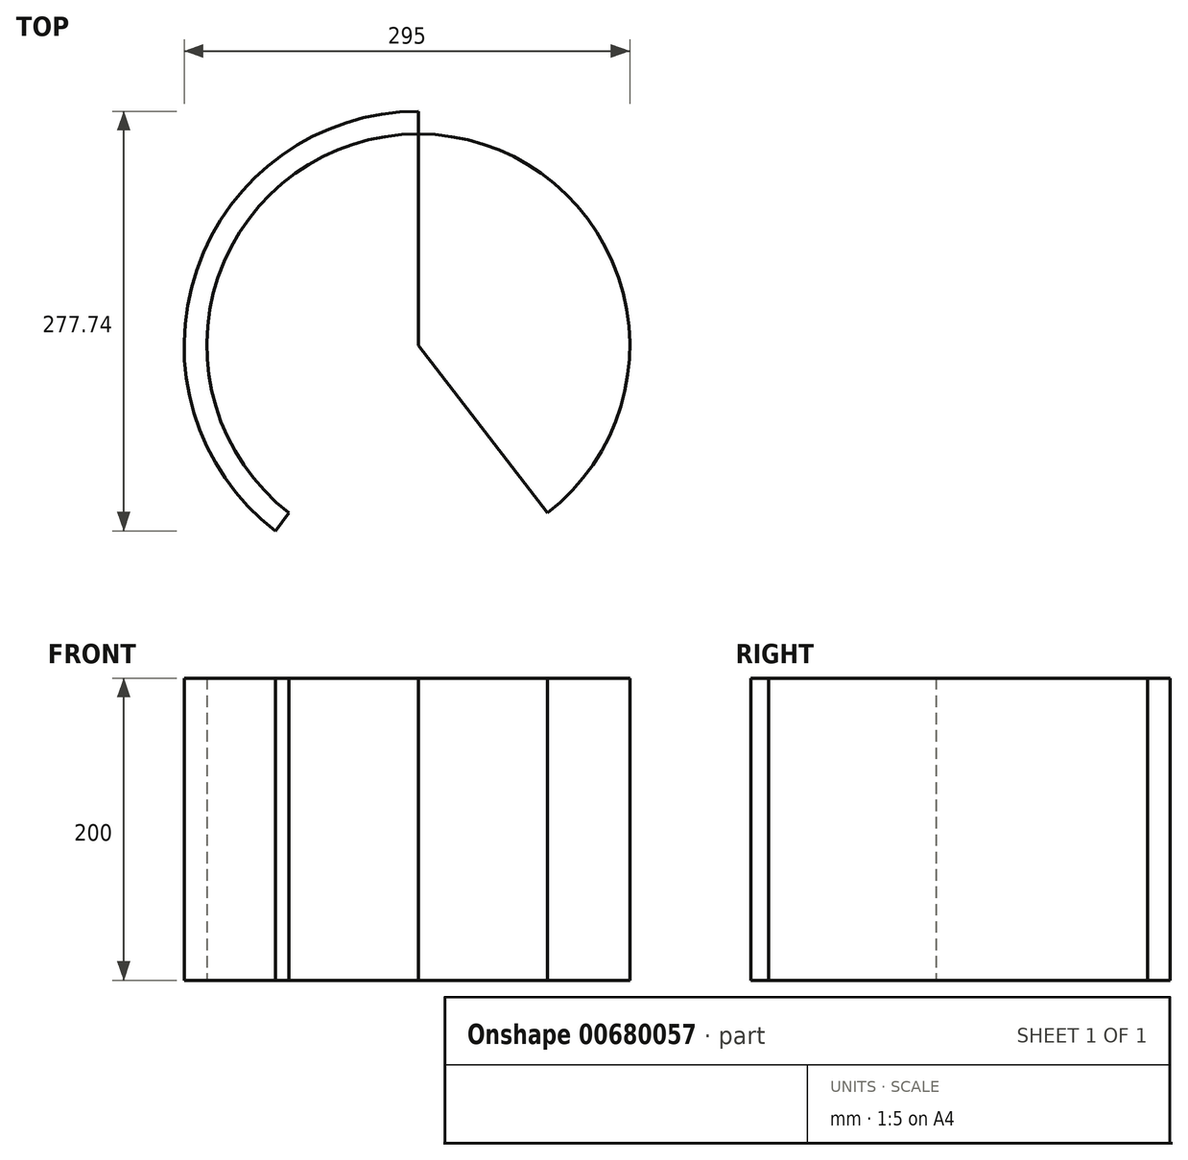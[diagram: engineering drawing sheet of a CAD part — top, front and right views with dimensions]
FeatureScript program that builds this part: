
annotation { "Feature Type Name" : "Feature", "Feature Type Description" : "" }
export const myFeature = defineFeature(function(context is Context, id is Id, definition is map)
    precondition{}
    {
        {
            var Q0;
            Q0=qCreatedBy(makeId("Top.planeOp"),FACE);
            var sketch = newSketch(context, id + "F0", { "sketchPlane" : qUnion([Q0])});
            skArc(sketch, "E0", {"start": v(-94.65, 122.74) * mm, "mid": v(-155, 0) * mm, "end": v(-94.65, -122.74) * mm});
            skArc(sketch, "E1", {"start": v(-85.5, 110.86) * mm, "mid": v(-140, 0) * mm, "end": v(-85.5, -110.86) * mm});
            skLineSegment(sketch, "E2", {"start": v(0, 0) * mm, "end": v(0, 155) * mm});
            skLineSegment(sketch, "E3", {"start": v(0, 155) * mm, "end": v(0, 0) * mm});
            skLineSegment(sketch, "E4", {"start": v(0, 0) * mm, "end": v(0, -155) * mm});
            skLineSegment(sketch, "E5", {"start": v(0, 0) * mm, "end": v(-94.65, -122.74) * mm});
            skArc(sketch, "E6", {"start": v(0, 155) * mm, "mid": v(-146.71, 50) * mm, "end": v(-94.65, -122.74) * mm});
            skArc(sketch, "E7", {"start": v(0, 140) * mm, "mid": v(-132.52, 45.16) * mm, "end": v(-85.5, -110.86) * mm});
            skArc(sketch, "E8.MirrorCS", {"start": v(0, 140) * mm, "mid": v(132.52, 45.16) * mm, "end": v(85.5, -110.86) * mm});
            skArc(sketch, "E9.MirrorCS", {"start": v(0, 155) * mm, "mid": v(146.71, 50) * mm, "end": v(94.65, -122.74) * mm});
            skLineSegment(sketch, "E10.MirrorCS", {"start": v(0, 0) * mm, "end": v(94.65, -122.74) * mm});
            skSolve(sketch);
        }
        {
            var Q0;
            {var subQ0=sQuery(id+"F0.wireOp",EDGE,"E0");Q0=makeQuery(id+"F0.imprint","IMPRINT",FACE,{"disambiguationData":[TD([[makeQuery(id+"F0.imprint","IMPRINT",EDGE,{"derivedFrom":subQ0}),1.0]])]});}
            var Q1;
            {var subQ5=sQuery(id+"F0.wireOp",EDGE,"E7");var subQ8=makeQuery(id+"F0.imprint","IMPRINT",VERTEX,{"derivedFrom":subQ5});Q1=makeQuery(id+"F0.imprint","IMPRINT",FACE,{"disambiguationData":[TD([[makeQuery(id+"F0.imprint","IMPRINT",EDGE,{"disambiguationData":[TD([[subQ8,1.0]])],"derivedFrom":subQ5}),-1.0]])]});}
            var Q2;
            {var subQ2=sQuery(id+"F0.wireOp",EDGE,"E8.MirrorCS");Q2=makeQuery(id+"F0.imprint","IMPRINT",FACE,{"disambiguationData":[TD([[makeQuery(id+"F0.imprint","IMPRINT",EDGE,{"derivedFrom":subQ2}),1.0]])]});}
            extrude(context, id + "F1", {"entities" : qUnion([Q0, Q1, Q2]), "depth" : 200 * mm});
        }
    });
